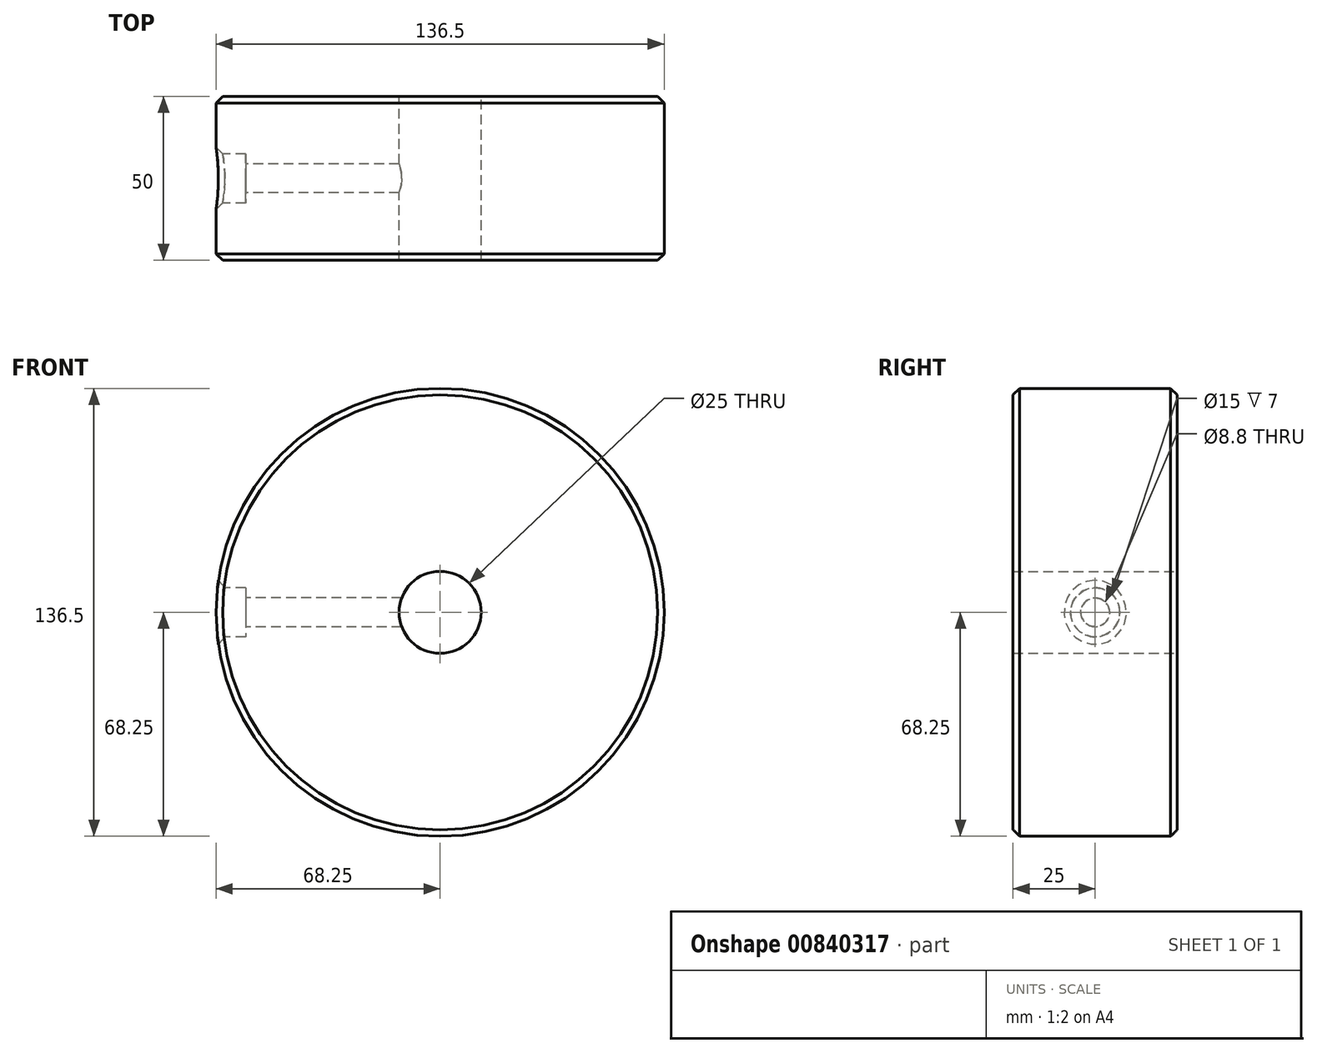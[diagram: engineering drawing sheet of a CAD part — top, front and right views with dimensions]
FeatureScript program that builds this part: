
annotation { "Feature Type Name" : "Feature", "Feature Type Description" : "" }
export const myFeature = defineFeature(function(context is Context, id is Id, definition is map)
    precondition{}
    {
        {
            var Q0;
            Q0=qCreatedBy(makeId("Front.planeOp"),FACE);
            var sketch = newSketch(context, id + "F0", { "sketchPlane" : qUnion([Q0])});
            skCircle(sketch, "E0", {"center": v(0, 0) * mm, "radius": 68.25 * mm});
            skCircle(sketch, "E1", {"center": v(0, 0) * mm, "radius": 12.5 * mm});
            skSolve(sketch);
        }
        {
            var Q0;
            Q0 = qSketchRegion(id + "F0", true);
            extrude(context, id + "F1", {"entities" : qUnion([Q0]), "endBound" : BoundingType.SYMMETRIC, "depth" : 50 * mm, "offsetDistance" : 25 * mm});
        }
        {
            var Q0;
            Q0=qCreatedBy(makeId("Right.planeOp"),FACE);
            cPlane(context, id + "F2", {"entities" : qUnion([Q0]), "cplaneType" : CPlaneType.OFFSET, "offset" : (136.5 / 2) * mm, "oppositeDirection" : true, "width" : 150 * mm, "height" : 150 * mm});
        }
        {
            var Q0;
            Q0=qCreatedBy(id+"F2.planeOp",FACE);
            var sketch = newSketch(context, id + "F3", { "sketchPlane" : qUnion([Q0])});
            skPoint(sketch, "E2", {"position": v(0, 0) * mm});
            skSolve(sketch);
        }
        {
            var Q0;
            Q0=sQuery(id+"F3.wireOp",VERTEX,"E2");
            var Q1;
            Q1=makeQuery(id+"F1.opExtrude","SWEPT_BODY",BODY,{"disambiguationData":[OSD([sQuery(id+"F0.wireOp",EDGE,"E0"),sQuery(id+"F0.wireOp",EDGE,"E1")])]});
            hole(context, id + "F4", {"style" : HoleStyle.C_BORE, "endStyle" : HoleEndStyle.BLIND, "oppositeDirection" : true, "holeDiameter" : 8.8 * mm, "cBoreDiameter" : 15 * mm, "cBoreDepth" : 9 * mm, "majorDiameter" : 5 * mm, "holeDepth" : 70 * mm, "isTappedThrough" : true, "tappedDepth" : 20 * mm, "tapClearance" : 3, "startFromSketch" : true, "locations" : qUnion([Q0]), "scope" : qUnion([Q1])});
        }
        {
            var Q0;
            Q0=makeQuery(id+"F1.opExtrude","SWEPT_FACE",FACE,{"disambiguationData":[OSD([sQuery(id+"F0.wireOp",EDGE,"E0")])]});
            chamfer(context, id + "F5", {"entities" : qUnion([Q0]), "width" : 2 * mm, "tangentPropagation" : true});
        }
    });
